# Revit family: E-712_RFA
name_source: partatom
category: Aparatos sanitarios
units: mm (PartAtom-declared; Revit-internal decimal feet)

## family parameters
Activar corte en vistas = No
Compartido = Sí
Corte con vacíos al cargar = No
Cota de conector redondo = Usar diámetro
Mantener orientación de anotación = No
Número OmniClass = 23.45.55.14
Punto de cálculo de habitación = Sí
Se basa en plano de trabajo = Sí
Siempre vertical = Sí
Tipo de pieza = Normal
Título OmniClass = Single Faucets

## types (1)
- E-712
    Accesorios = Llave allen 5/64".
Llave hexagonal. Llave hexagonal.
    Características = Cartucho de 35 mm
    Descripción = Monomando para Regadera o Tina sin Desviador
    Diámetro = 4"
    Elevación por defecto = 47"
    Fabricante = HELVEX S.A. DE C.V.
    Imagen de tipo = E-712.PNG
    Instalación = Conexión interna de 1/2"-14 NPT para agua fría (azul). Conexión interna de 1/2"-14 NPT para agua caliente (rojo). Conexión interna de 1/2"-14 NPT de salida (negro).
    Material = Brass
    Modelo = E-712
    Operación = Para abrir el flujo de agua levante la palanca maneral y gire para regular la temperatura.
    Presión máxima de trabajo = 85.3 psi
    Presión mínima de trabajo = 11.4 psi
    Total Height = 5"
    URL = https://helvex.com.mx

## geometry (parser evidence)
native form markers: Sweep x3
no freeform markers — native parametric forms only
